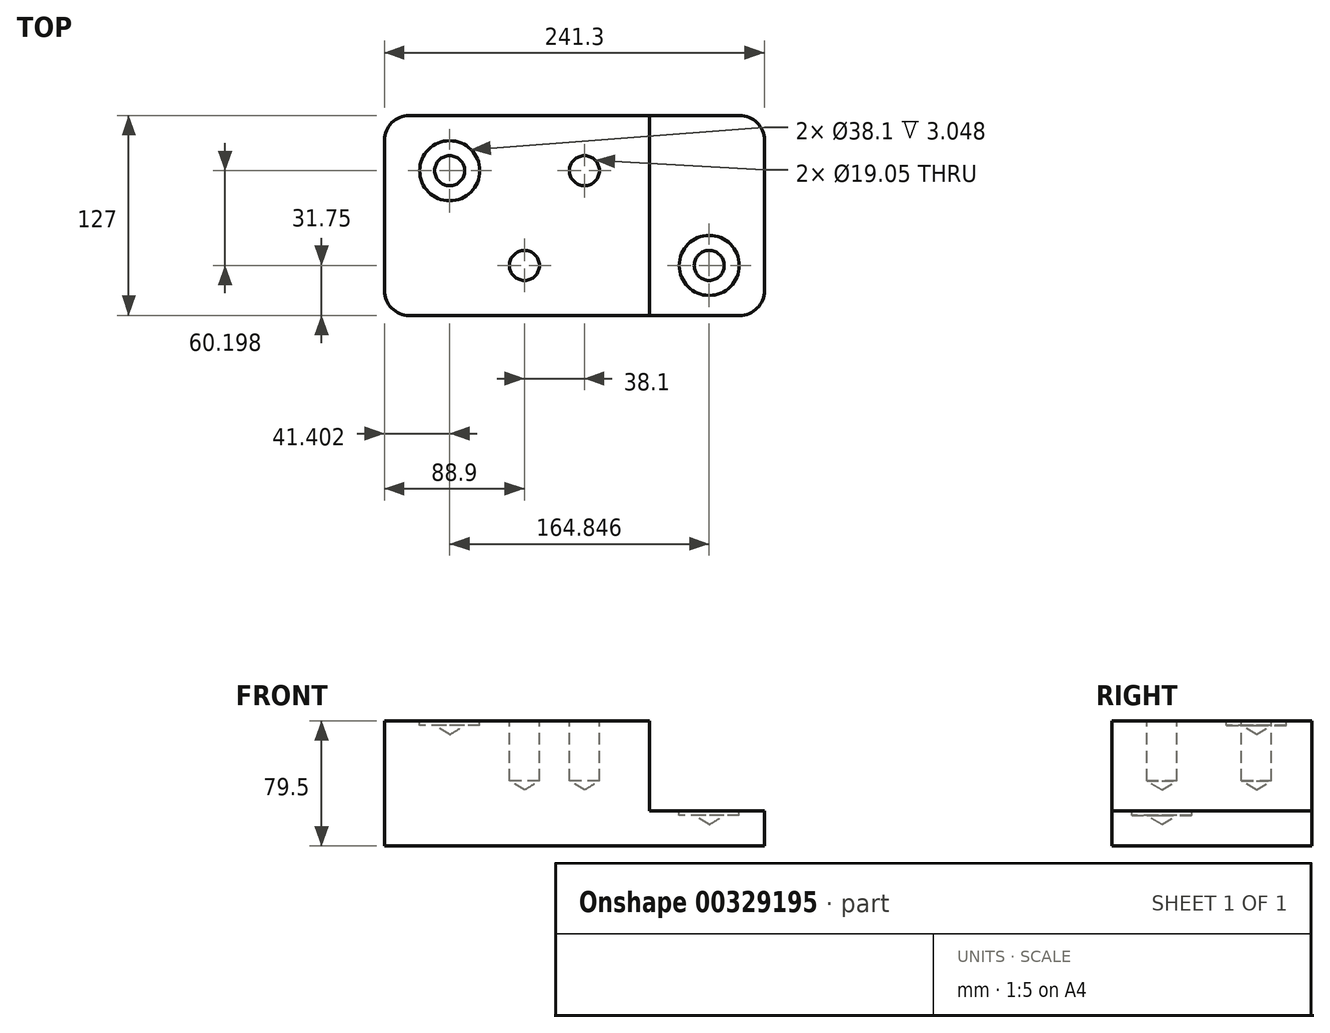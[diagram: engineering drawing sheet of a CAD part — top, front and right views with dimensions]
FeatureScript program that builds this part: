
annotation { "Feature Type Name" : "Feature", "Feature Type Description" : "" }
export const myFeature = defineFeature(function(context is Context, id is Id, definition is map)
    precondition{}
    {
        {
            var Q0;
            Q0=qCreatedBy(makeId("Front.planeOp"),FACE);
            var sketch = newSketch(context, id + "F0", { "sketchPlane" : qUnion([Q0])});
            skLineSegment(sketch, "E0.bottom", {"start": v(0, 0) * mm, "end": v(241.3, 0) * mm});
            skLineSegment(sketch, "E0.top", {"start": v(0, 79.5) * mm, "end": v(241.3, 79.5) * mm});
            skLineSegment(sketch, "E0.left", {"start": v(0, 0) * mm, "end": v(0, 79.5) * mm});
            skLineSegment(sketch, "E0.right", {"start": v(241.3, 0) * mm, "end": v(241.3, 79.5) * mm});
            skSolve(sketch);
        }
        {
            var Q0;
            Q0 = qSketchRegion(id + "F0", true);
            extrude(context, id + "F1", {"entities" : qUnion([Q0]), "depth" : 127 * mm});
        }
        {
            var Q0;
            Q0=makeQuery(id+"F1.opExtrude","SWEPT_FACE",FACE,{"disambiguationData":[OSD([sQuery(id+"F0.wireOp",EDGE,"E0.top")])]});
            var sketch = newSketch(context, id + "F2", { "sketchPlane" : qUnion([Q0])});
            skPoint(sketch, "E1.visualSharp", {"position": v(0, 0) * mm});
            skPoint(sketch, "E2.visualSharp", {"position": v(168.4, 0) * mm});
            skPoint(sketch, "E3.visualSharp", {"position": v(168.4, -127) * mm});
            skLineSegment(sketch, "E4", {"start": v(241.3, 0) * mm, "end": v(241.3, -127) * mm});
            skLineSegment(sketch, "E5.bottom", {"start": v(0, 0) * mm, "end": v(168.4, 0) * mm});
            skLineSegment(sketch, "E5.top", {"start": v(0, -127) * mm, "end": v(168.4, -127) * mm});
            skLineSegment(sketch, "E5.left", {"start": v(0, 0) * mm, "end": v(0, -127) * mm});
            skLineSegment(sketch, "E5.right", {"start": v(168.4, 0) * mm, "end": v(168.4, -127) * mm});
            skLineSegment(sketch, "E6", {"start": v(168.4, 0) * mm, "end": v(241.3, 0) * mm});
            skLineSegment(sketch, "E7", {"start": v(241.3, -127) * mm, "end": v(168.4, -127) * mm});
            skSolve(sketch);
        }
        {
            var Q0;
            Q0=makeQuery(id+"F2.imprint","IMPRINT",FACE,{"disambiguationData":[TD([[makeQuery(id+"F2.imprint","IMPRINT",EDGE,{"derivedFrom":sQuery(id+"F2.wireOp",EDGE,"RtnUJpqR-7f3k-g5HC-vRvu-F1PFgzHjxR6f.right")}),1.0]])]});
            var Q1;
            Q1=makeQuery(id+"F2.imprint","IMPRINT",FACE,{"disambiguationData":[TD([[makeQuery(id+"F2.imprint","IMPRINT",EDGE,{"derivedFrom":sQuery(id+"F2.wireOp",EDGE,"E4")}),1.0]])]});
            extrude(context, id + "F3", {"entities" : qUnion([Q0, Q1]), "operationType" : NewBodyOperationType.REMOVE, "oppositeDirection" : true, "depth" : 57.15 * mm});
        }
        {
            var Q0;
            Q0=makeQuery(id+"F2.imprint","IMPRINT",FACE,{"disambiguationData":[TD([[makeQuery(id+"F2.imprint","IMPRINT",EDGE,{"derivedFrom":sQuery(id+"F2.wireOp",EDGE,"E5.bottom")}),-1.0]])]});
            var sketch = newSketch(context, id + "F4", { "sketchPlane" : qUnion([Q0])});
            skCircle(sketch, "E8", {"center": v(41.4, -35.05) * mm, "radius": 9.53 * mm});
            skCircle(sketch, "E9", {"center": v(127, -35.05) * mm, "radius": 9.53 * mm});
            skCircle(sketch, "E10", {"center": v(88.9, -95.25) * mm, "radius": 9.53 * mm});
            skCircle(sketch, "E11", {"center": v(206.25, -95.25) * mm, "radius": 9.53 * mm});
            skSolve(sketch);
        }
        {
            var Q0;
            Q0=sQuery(id+"F4.wireOp",VERTEX,"E8.center");
            var Q1;
            Q1=sQuery(id+"F4.wireOp",VERTEX,"E11.center");
            var Q2;
            Q2=makeQuery(id+"F1.opExtrude","SWEPT_BODY",BODY,{"disambiguationData":[OSD([sQuery(id+"F0.wireOp",EDGE,"E0.bottom"),sQuery(id+"F0.wireOp",EDGE,"E0.top"),sQuery(id+"F0.wireOp",EDGE,"E0.left"),sQuery(id+"F0.wireOp",EDGE,"E0.right")])]});
            hole(context, id + "F5", {"style" : HoleStyle.C_BORE, "endStyle" : HoleEndStyle.BLIND, "holeDiameter" : 19.05 * mm, "cBoreDiameter" : 38.1 * mm, "cBoreDepth" : 3.05 * mm, "holeDepth" : 3.05 * mm, "tappedDepth" : 12.7 * mm, "tapClearance" : 3, "locations" : qUnion([Q0, Q1]), "scope" : qUnion([Q2])});
        }
        {
            var Q0;
            Q0=sQuery(id+"F4.wireOp",VERTEX,"E10.center");
            var Q1;
            Q1=sQuery(id+"F4.wireOp",VERTEX,"E9.center");
            var Q2;
            Q2=makeQuery(id+"F1.opExtrude","SWEPT_BODY",BODY,{"disambiguationData":[OSD([sQuery(id+"F0.wireOp",EDGE,"E0.bottom"),sQuery(id+"F0.wireOp",EDGE,"E0.top"),sQuery(id+"F0.wireOp",EDGE,"E0.left"),sQuery(id+"F0.wireOp",EDGE,"E0.right")])]});
            hole(context, id + "F6", {"style" : HoleStyle.C_SINK, "endStyle" : HoleEndStyle.BLIND, "holeDiameter" : 19.05 * mm, "cSinkDiameter" : 19.05 * mm, "cSinkAngle" : 82 * degree, "holeDepth" : 38.1 * mm, "tappedDepth" : 12.7 * mm, "tapClearance" : 3, "locations" : qUnion([Q0, Q1]), "scope" : qUnion([Q2])});
        }
        {
            var Q0;
            Q0=makeQuery(id+"F3.boolean.opBoolean","COPY",EDGE,{"derivedFrom":makeQuery(id+"F3.opExtrude","SWEPT_EDGE",EDGE,{"disambiguationData":[OSD([sQuery(id+"F2.wireOp",EDGE,"E5.top"),sQuery(id+"F2.wireOp",EDGE,"E5.right"),sQuery(id+"F2.wireOp",EDGE,"E7")])]})});
            var Q1;
            Q1=makeQuery(id+"F3.boolean.opBoolean","COPY",EDGE,{"derivedFrom":makeQuery(id+"F3.opExtrude","SWEPT_EDGE",EDGE,{"disambiguationData":[OSD([sQuery(id+"F2.wireOp",EDGE,"E5.bottom"),sQuery(id+"F2.wireOp",EDGE,"E5.right"),sQuery(id+"F2.wireOp",EDGE,"E6")])]})});
            var Q2;
            Q2=makeQuery(id+"F1.opExtrude","CAP_EDGE",EDGE,{"disambiguationData":[OSD([sQuery(id+"F0.wireOp",EDGE,"E0.right")])],"isStart":false});
            var Q3;
            Q3=makeQuery(id+"F1.opExtrude","CAP_EDGE",EDGE,{"disambiguationData":[OSD([sQuery(id+"F0.wireOp",EDGE,"E0.right")])],"isStart":true});
            var Q4;
            Q4=makeQuery(id+"F1.opExtrude","CAP_EDGE",EDGE,{"disambiguationData":[OSD([sQuery(id+"F0.wireOp",EDGE,"E0.left")])],"isStart":false});
            var Q5;
            Q5=makeQuery(id+"F1.opExtrude","CAP_EDGE",EDGE,{"disambiguationData":[OSD([sQuery(id+"F0.wireOp",EDGE,"E0.left")])],"isStart":true});
            fillet(context, id + "F7", {"entities" : qUnion([Q0, Q1, Q2, Q3, Q4, Q5]), "radius" : 15.75 * mm, "tangentPropagation" : true, "allowEdgeOverflow" : false});
        }
    });
